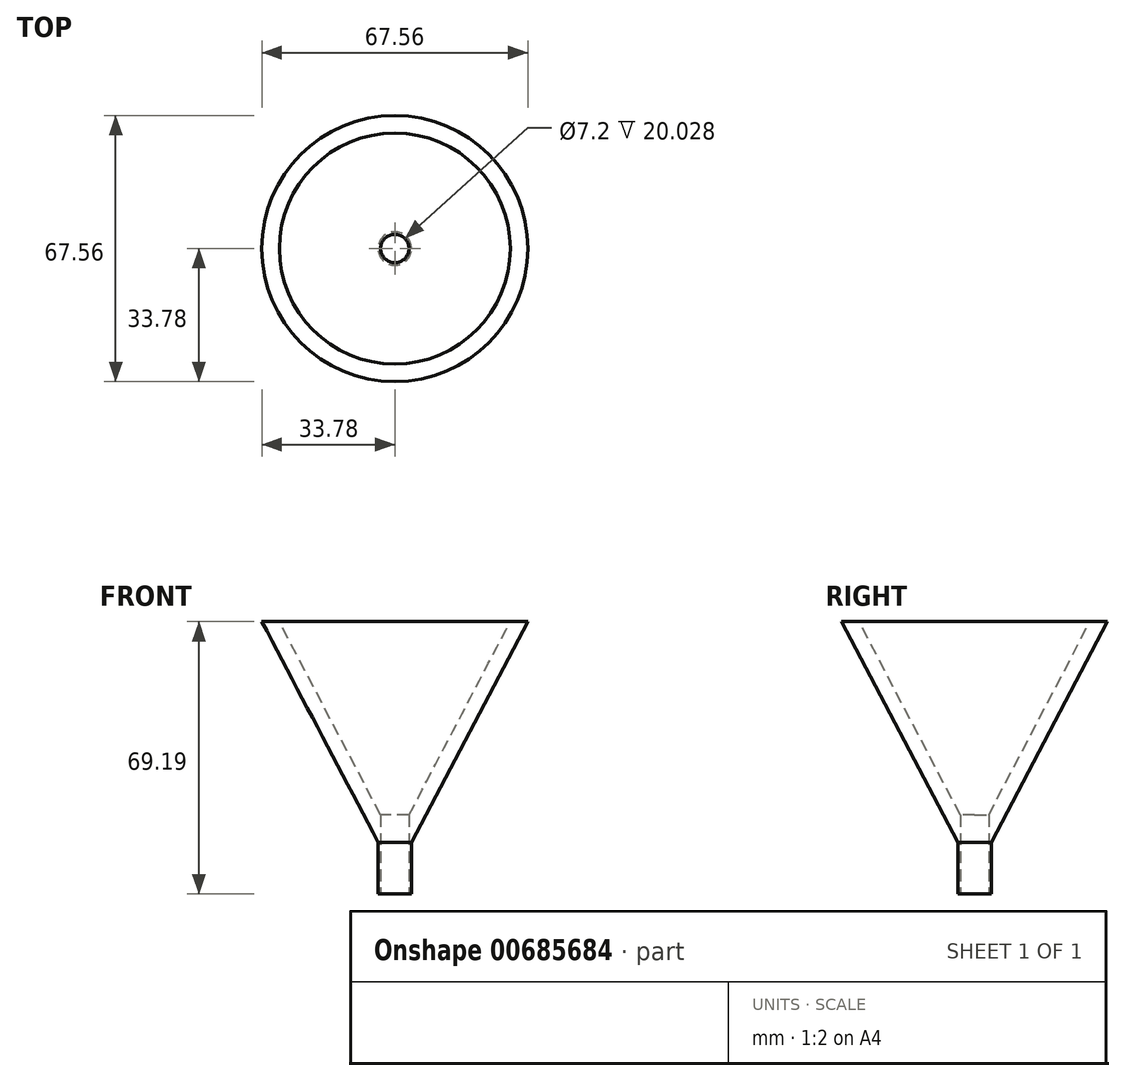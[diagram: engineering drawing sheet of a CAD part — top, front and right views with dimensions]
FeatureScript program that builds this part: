
annotation { "Feature Type Name" : "Feature", "Feature Type Description" : "" }
export const myFeature = defineFeature(function(context is Context, id is Id, definition is map)
    precondition{}
    {
        {
            var Q0;
            Q0=qCreatedBy(makeId("Front.planeOp"),FACE);
            var sketch = newSketch(context, id + "F0", { "sketchPlane" : qUnion([Q0])});
            skLineSegment(sketch, "E0", {"start": v(29.33, 56.04) * mm, "end": v(33.78, 56.04) * mm});
            skLineSegment(sketch, "E1", {"start": v(33.78, 56.04) * mm, "end": v(4.25, 0) * mm});
            skLineSegment(sketch, "E2", {"start": v(4.25, 0) * mm, "end": v(4.25, -13.15) * mm});
            skLineSegment(sketch, "E3", {"start": v(4.25, -13.15) * mm, "end": v(0, -13.15) * mm});
            skLineSegment(sketch, "E4", {"start": v(0, -13.15) * mm, "end": v(0, 0) * mm});
            skLineSegment(sketch, "E5", {"start": v(0, 0) * mm, "end": v(29.33, 56.04) * mm});
            skSolve(sketch);
        }
        {
            var Q0;
            Q0 = qSketchRegion(id + "F0", true);
            var Q1;
            Q1=sQuery(id+"F0.wireOp",EDGE,"E4");
            revolve(context, id + "F1", {"surfaceOperationType" : NewSurfaceOperationType.NEW, "entities" : qUnion([Q0]), "axis" : qUnion([Q1]), "revolveType" : RevolveType.FULL});
        }
        {
            var Q0;
            Q0=makeQuery(id+"F1.opRevolve","SWEPT_FACE",FACE,{"disambiguationData":[OSD([sQuery(id+"F0.wireOp",EDGE,"E3")])]});
            var sketch = newSketch(context, id + "F2", { "sketchPlane" : qUnion([Q0])});
            skCircle(sketch, "E6", {"center": v(0, 0) * mm, "radius": 3.6 * mm});
            skSolve(sketch);
        }
        {
            var Q0;
            Q0 = qSketchRegion(id + "F2", true);
            extrude(context, id + "F3", {"entities" : qUnion([Q0]), "operationType" : NewBodyOperationType.REMOVE, "oppositeDirection" : true, "depth" : 25.4 * mm, "offsetDistance" : 25.4 * mm});
        }
    });
